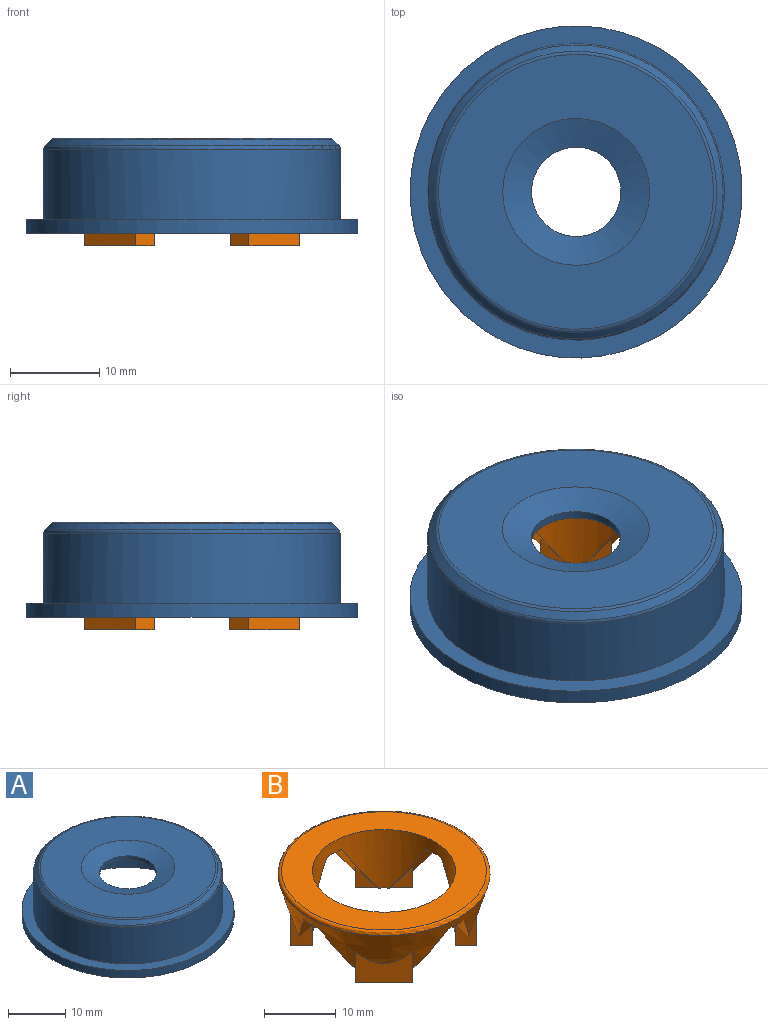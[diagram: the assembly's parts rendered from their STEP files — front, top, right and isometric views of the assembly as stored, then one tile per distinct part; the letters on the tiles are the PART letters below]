
ASSEMBLY  parts=2 mates=1
PART A: 14 faces, bbox 37.2x37.2x10.7 mm
  f0: plane 20x20mm, normal (0,0,-1), area 235.6mm2, adj f3,f10
  f1: plane 37.2x37.2mm, normal (0,0,-1), area 380mm2, adj f2,f8
  f2: cylinder r=15mm len=30mm, axis (0,0,-1), area 910.2mm2, adj f1,f9
  f3: cylinder r=5mm len=10mm, axis (0,0,-1), area 27.8mm2, adj f0,f4
  f4: cone r=8.22mm half-angle=70.9deg, axis (0,0,1), area 141.6mm2, adj f3,f5
  f5: plane 30.79x30.79mm, normal (0,0,1), area 532mm2, adj f4,f12
  f6: cylinder r=16.6mm len=33.2mm, axis (0,0,-1), area 818.8mm2, adj f7,f13
  f7: plane 37.2x37.2mm, normal (0,0,1), area 221.2mm2, adj f6,f8
  f8: cylinder r=18.6mm len=37.2mm, axis (0,0,-1), area 187mm2, adj f1,f7
  f9: plane 30x30mm, normal (0,0,-1), area 91.1mm2, adj f2,f10
  f10: cone r=10mm half-angle=76deg, axis (0,0,1), area 310.9mm2, adj f0,f9
  f11: cone r=16.6mm half-angle=45deg, axis (0,0,-1), area 101.2mm2, adj f12,f13
  f12: torus R=15.39mm, axis (0,0,1), area 38.4mm2, adj f5,f11
  f13: torus R=16.1mm, axis (0,0,1), area 40.8mm2, adj f6,f11
PART B: 40 faces, bbox 32.1x32.1x10 mm
  f0: cone r=15mm half-angle=16.7deg, axis (0,0,1), area 421.6mm2, adj f1,f2,f3,f4,f5,f6,f7,f14
  f1: plane 8x6.72mm, normal (0.85,0,-0.53), area 24.6mm2, adj f0,f8,f11,f15,f35,f36
  f2: plane 8x6.72mm, normal (0,0.85,-0.53), area 24.6mm2, adj f0,f8,f11,f16,f37,f38
  f3: plane 8x6.72mm, normal (-0.85,0,-0.53), area 24.6mm2, adj f0,f10,f11,f15,f30,f31
  f4: plane 8x6.72mm, normal (0,0.85,-0.53), area 24.6mm2, adj f0,f10,f11,f14,f32,f33
  f5: plane 8x6.72mm, normal (0,-0.85,-0.53), area 24.6mm2, adj f0,f11,f12,f14,f25,f26
  f6: plane 8x6.72mm, normal (-0.85,0,-0.53), area 24.6mm2, adj f0,f11,f12,f17,f27,f28
  f7: plane 8x6.72mm, normal (0,-0.85,-0.53), area 24.6mm2, adj f0,f9,f11,f16,f22,f23
  f8: plane 7.78x7.78mm, normal (0,0,-1), area 24mm2, adj f1,f2,f11,f34,f35,f36,f37,f38
  f9: plane 7.78x7.78mm, normal (0,0,-1), area 24mm2, adj f7,f11,f18,f19,f20,f21,f22,f23
  f10: plane 7.78x7.78mm, normal (0,0,-1), area 24mm2, adj f3,f4,f11,f29,f30,f31,f32,f33
  f11: cylinder r=10mm len=20mm, axis (0,0,-1), area 361.3mm2, adj f1,f2,f3,f4,f5,f6,f7,f8
  f12: plane 7.78x7.78mm, normal (0,0,-1), area 24mm2, adj f5,f6,f11,f24,f25,f26,f27,f28
  f13: plane 28.66x28.66mm, normal (0,0,1), area 330.8mm2, adj f11,f39
  f14: plane 4.51x3mm, normal (0,0,-1), area 13.2mm2, adj f0,f4,f5,f11
  f15: plane 4.51x3mm, normal (0,0,-1), area 13.2mm2, adj f0,f1,f3,f11
  f16: plane 4.51x3mm, normal (0,0,-1), area 13.2mm2, adj f0,f2,f7,f11
  f17: plane 4.51x3mm, normal (0,0,-1), area 13.2mm2, adj f0,f6,f11,f18
  f18: plane 8x6.72mm, normal (0.85,0,-0.53), area 24.6mm2, adj f0,f9,f11,f17,f20,f21
  f19: plane 5.66x5.66mm, normal (-0.71,0.71,0), area 32.1mm2, adj f0,f9,f20,f22
  f20: plane 5.36x2.14mm, normal (0.71,0.71,0), area 8.8mm2, adj f0,f9,f18,f19,f21
  f21: plane 3.61x2.26mm, normal (0.71,-0.71,0), area 5.8mm2, adj f9,f18,f20
  f22: plane 5.36x2.14mm, normal (-0.71,-0.71,0), area 8.8mm2, adj f0,f7,f9,f19,f23
  f23: plane 3.61x2.26mm, normal (0.71,-0.71,0), area 5.8mm2, adj f7,f9,f22
  f24: plane 5.66x5.66mm, normal (0.71,0.71,0), area 32.1mm2, adj f0,f12,f25,f27
  f25: plane 5.36x2.14mm, normal (0.71,-0.71,0), area 8.8mm2, adj f0,f5,f12,f24,f26
  f26: plane 3.61x2.26mm, normal (-0.71,-0.71,0), area 5.8mm2, adj f5,f12,f25
  f27: plane 5.36x2.14mm, normal (-0.71,0.71,0), area 8.8mm2, adj f0,f6,f12,f24,f28
  f28: plane 3.61x2.26mm, normal (-0.71,-0.71,0), area 5.8mm2, adj f6,f12,f27
  f29: plane 5.66x5.66mm, normal (0.71,-0.71,0), area 32.1mm2, adj f0,f10,f30,f32
  f30: plane 5.36x2.14mm, normal (-0.71,-0.71,0), area 8.8mm2, adj f0,f3,f10,f29,f31
  f31: plane 3.61x2.26mm, normal (-0.71,0.71,0), area 5.8mm2, adj f3,f10,f30
  f32: plane 5.36x2.14mm, normal (0.71,0.71,0), area 8.8mm2, adj f0,f4,f10,f29,f33
  f33: plane 3.61x2.26mm, normal (-0.71,0.71,0), area 5.8mm2, adj f4,f10,f32
  f34: plane 5.66x5.66mm, normal (-0.71,-0.71,0), area 32.1mm2, adj f0,f8,f35,f37
  f35: plane 5.36x2.14mm, normal (0.71,-0.71,0), area 8.8mm2, adj f0,f1,f8,f34,f36
  f36: plane 3.61x2.26mm, normal (0.71,0.71,0), area 5.8mm2, adj f1,f8,f35
  f37: plane 5.36x2.14mm, normal (-0.71,0.71,0), area 8.8mm2, adj f0,f2,f8,f34,f38
  f38: plane 3.61x2.26mm, normal (0.71,0.71,0), area 5.8mm2, adj f2,f8,f37
  f39: torus R=14.33mm, axis (0,0,-1), area 85.8mm2, adj f0,f13
PLACE A t=(0,0,1.37)mm
PLACE B at identity
MATE cylindrical A.f2 <-> B.f0  axis (0,0,-1) through (0,0,10.91)mm
